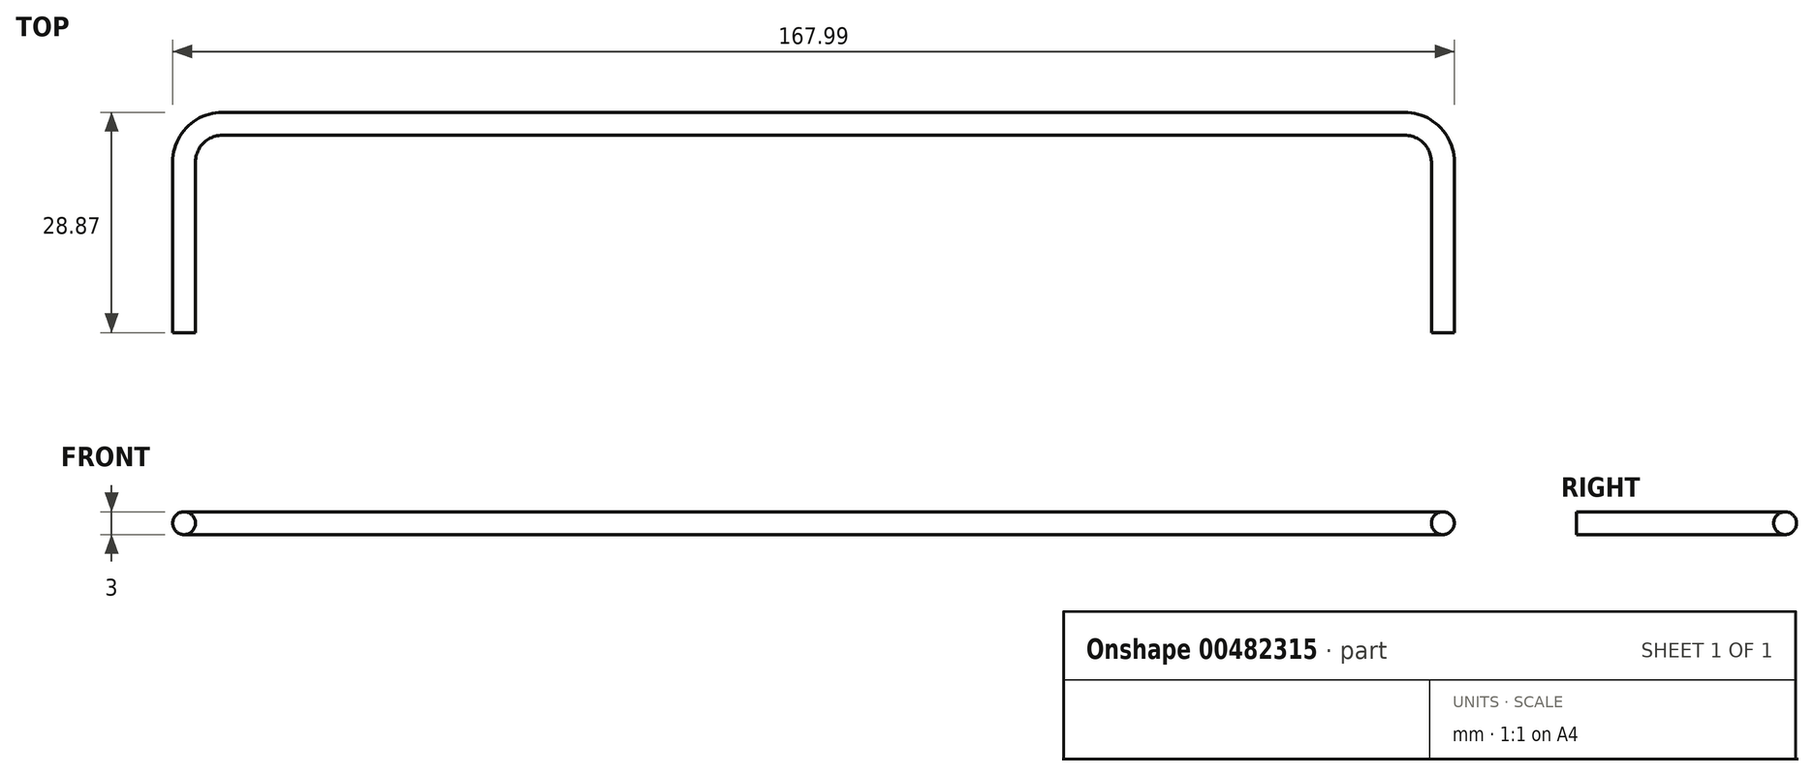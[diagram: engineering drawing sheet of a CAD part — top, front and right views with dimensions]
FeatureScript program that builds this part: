
annotation { "Feature Type Name" : "Feature", "Feature Type Description" : "" }
export const myFeature = defineFeature(function(context is Context, id is Id, definition is map)
    precondition{}
    {
        {
            var Q0;
            Q0=qCreatedBy(makeId("Top.planeOp"),FACE);
            var sketch = newSketch(context, id + "F0", { "sketchPlane" : qUnion([Q0])});
            skLineSegment(sketch, "E0", {"start": v(-46.44, 36.1) * mm, "end": v(108.56, 36.1) * mm});
            skLineSegment(sketch, "E1", {"start": v(113.56, 31.1) * mm, "end": v(113.56, 8.72) * mm});
            skLineSegment(sketch, "E2", {"start": v(-51.44, 31.1) * mm, "end": v(-51.44, 8.72) * mm});
            skPoint(sketch, "E3.visualSharp", {"position": v(-51.44, 36.1) * mm});
            skArc(sketch, "E3.filletArc", {"start": v(-46.44, 36.1) * mm, "mid": v(-49.97, 34.63) * mm, "end": v(-51.44, 31.1) * mm});
            skPoint(sketch, "E4.visualSharp", {"position": v(113.56, 36.1) * mm});
            skArc(sketch, "E4.filletArc", {"start": v(113.56, 31.1) * mm, "mid": v(112.1, 34.63) * mm, "end": v(108.56, 36.1) * mm});
            skLineSegment(sketch, "E5", {"start": v(113.56, 8.72) * mm, "end": v(104.8, 8.72) * mm});
            skSolve(sketch);
        }
        {
            var Q0;
            Q0=qCreatedBy(id+"FqiWXO5US18zetI.pointOp",VERTEX);
            var Q1;
            Q1=sQuery(id+"F0.wireOp",EDGE,"E5");
            cPlane(context, id + "F1", {"entities" : qUnion([Q0, Q1]), "cplaneType" : CPlaneType.LINE_ANGLE, "offset" : 25 * mm, "angle" : 0 * degree, "width" : 150 * mm, "height" : 150 * mm});
        }
        {
            var Q0;
            Q0=sQuery(id+"F0.wireOp",EDGE,"E5");
            cPlane(context, id + "F2", {"entities" : qUnion([Q0]), "cplaneType" : CPlaneType.LINE_ANGLE, "offset" : 25 * mm, "angle" : 0 * degree, "width" : 150 * mm, "height" : 150 * mm});
        }
        {
            var Q0;
            Q0=qCreatedBy(id+"F2.planeOp",FACE);
            var sketch = newSketch(context, id + "F3", { "sketchPlane" : qUnion([Q0])});
            skCircle(sketch, "E6", {"center": v(1115.96, 0) * mm, "radius": 0.1 * mm});
            skCircle(sketch, "E7", {"center": v(113.56, 0) * mm, "radius": 1.5 * mm});
            skSolve(sketch);
        }
        {
            var Q0;
            Q0=makeQuery(id+"F3.imprint","IMPRINT",FACE,{"disambiguationData":[TD([[makeQuery(id+"F3.imprint","IMPRINT",EDGE,{"derivedFrom":sQuery(id+"F3.wireOp",EDGE,"E7")}),1.0]])]});
            var Q1;
            Q1=sQuery(id+"F0.wireOp",EDGE,"E1");
            var Q2;
            Q2=sQuery(id+"F0.wireOp",EDGE,"E4.filletArc");
            var Q3;
            Q3=sQuery(id+"F0.wireOp",EDGE,"E0");
            var Q4;
            Q4=sQuery(id+"F0.wireOp",EDGE,"E3.filletArc");
            var Q5;
            Q5=sQuery(id+"F0.wireOp",EDGE,"E2");
            sweep(context, id + "F4", {"profiles" : qUnion([Q0]), "path" : qUnion([Q1, Q2, Q3, Q4, Q5])});
        }
    });
